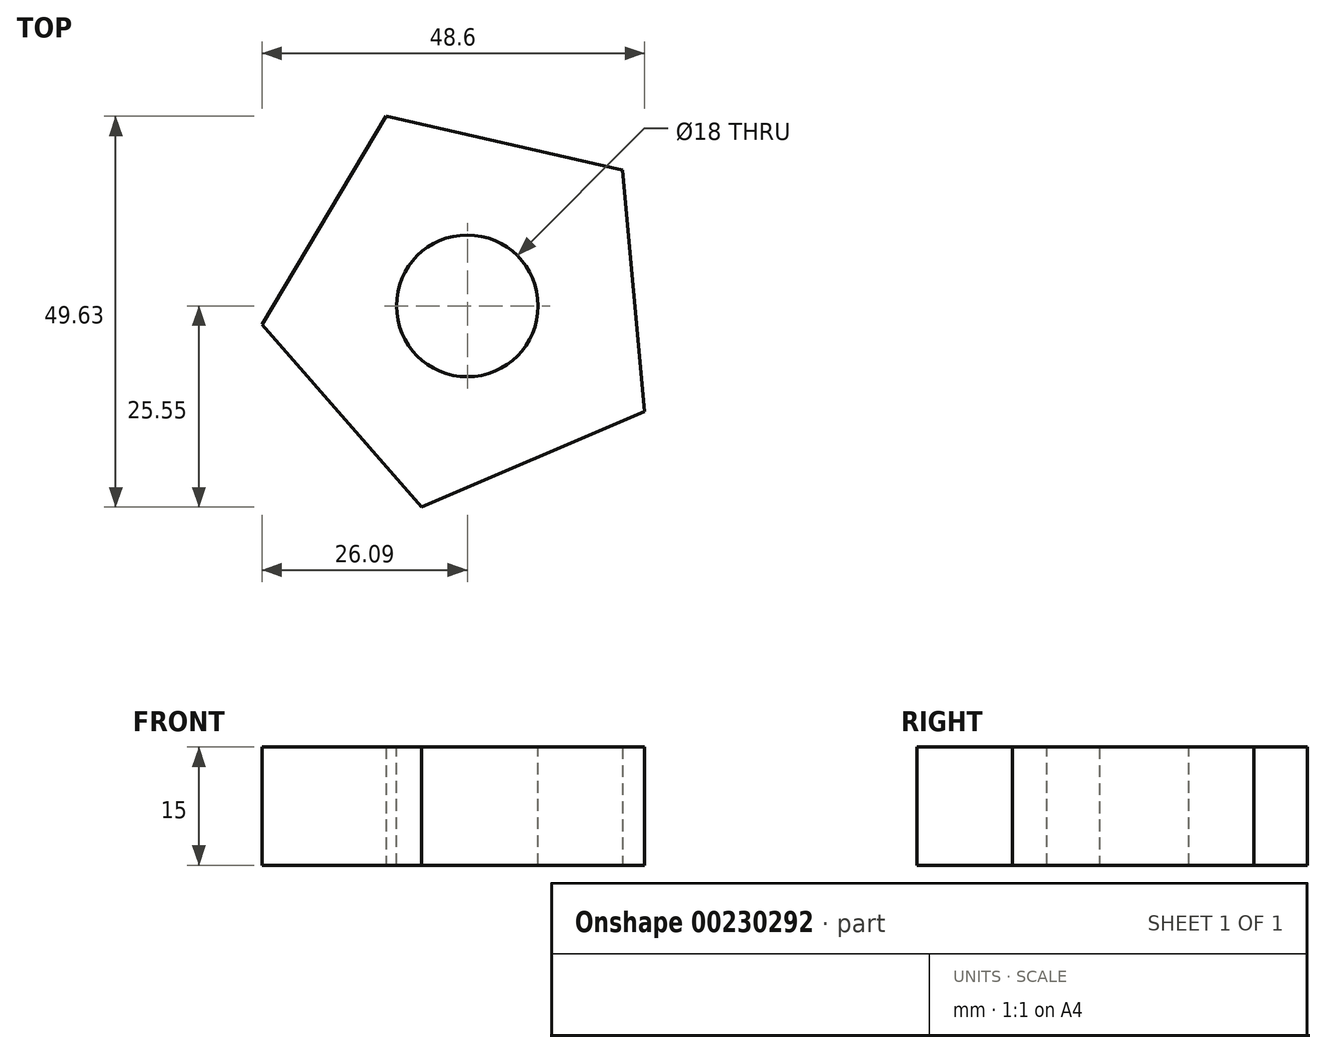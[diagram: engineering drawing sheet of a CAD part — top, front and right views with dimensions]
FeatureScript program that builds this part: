
annotation { "Feature Type Name" : "Feature", "Feature Type Description" : "" }
export const myFeature = defineFeature(function(context is Context, id is Id, definition is map)
    precondition{}
    {
        {
            var Q0;
            Q0=qCreatedBy(makeId("Top.planeOp"),FACE);
            var sketch = newSketch(context, id + "F0", { "sketchPlane" : qUnion([Q0])});
            skCircle(sketch, "E0.cCircle", {"center": v(0, 0) * mm, "radius": 26.2 * mm, "construction": true});
            skLineSegment(sketch, "E0.0", {"start": v(22.5, -13.41) * mm, "end": v(-5.8, -25.55) * mm});
            skLineSegment(sketch, "E0.1", {"start": v(-5.8, -25.55) * mm, "end": v(-26.1, -2.38) * mm});
            skLineSegment(sketch, "E0.2", {"start": v(-26.1, -2.38) * mm, "end": v(-10.32, 24.08) * mm});
            skLineSegment(sketch, "E0.3", {"start": v(-10.32, 24.08) * mm, "end": v(19.71, 17.26) * mm});
            skLineSegment(sketch, "E0.4", {"start": v(19.71, 17.26) * mm, "end": v(22.5, -13.41) * mm});
            skSolve(sketch);
        }
        {
            var Q0;
            Q0=makeQuery(id+"F0.imprint","IMPRINT",FACE,{"disambiguationData":[TD([[makeQuery(id+"F0.imprint","IMPRINT",EDGE,{"derivedFrom":sQuery(id+"F0.wireOp",EDGE,"E0.0")}),-1.0]])]});
            extrude(context, id + "F1", {"entities" : qUnion([Q0]), "depth" : 15 * mm});
        }
        {
            var Q0;
            Q0=makeQuery(id+"F1.opExtrude","CAP_FACE",FACE,{"disambiguationData":[OSD([sQuery(id+"F0.wireOp",EDGE,"E0.0"),sQuery(id+"F0.wireOp",EDGE,"E0.1"),sQuery(id+"F0.wireOp",EDGE,"E0.2"),sQuery(id+"F0.wireOp",EDGE,"E0.3"),sQuery(id+"F0.wireOp",EDGE,"E0.4")])],"isStart":false});
            var sketch = newSketch(context, id + "F2", { "sketchPlane" : qUnion([Q0])});
            skCircle(sketch, "E1", {"center": v(0, 0) * mm, "radius": 9 * mm});
            skSolve(sketch);
        }
        {
            var Q0;
            Q0=makeQuery(id+"F2.imprint","IMPRINT",FACE,{"disambiguationData":[TD([[makeQuery(id+"F2.imprint","IMPRINT",EDGE,{"derivedFrom":sQuery(id+"F2.wireOp",EDGE,"E1")}),1.0]])]});
            extrude(context, id + "F3", {"entities" : qUnion([Q0]), "operationType" : NewBodyOperationType.REMOVE, "oppositeDirection" : true, "depth" : 18 * mm});
        }
    });
